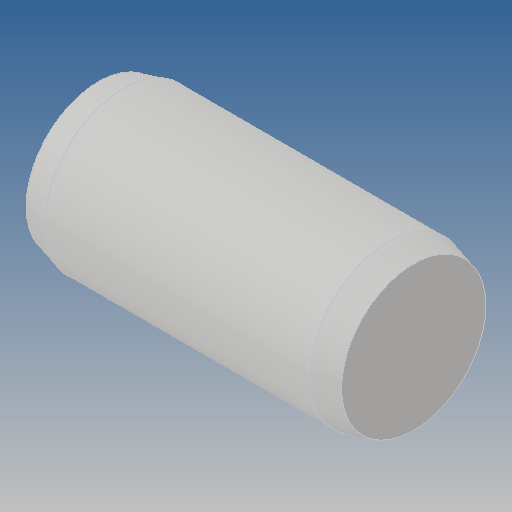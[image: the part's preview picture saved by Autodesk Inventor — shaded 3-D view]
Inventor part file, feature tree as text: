
AUTODESK INVENTOR PART (.ipt)
format: ipt  version: 2018 (Build 220112000, 112)  size: 109,056 bytes
history: native  units: mm
features: extrude x1
ambient origin geometry x8: Origin, YZ Plane, XZ Plane, XY Plane, X Axis, Y Axis, Z Axis, Center Point
bodies: Solid1 (feature_tree)
feature tree (1):
  extrude  "Extrude3"  [1 undecoded]
note: 1 required parameter value undecoded (feature->parameter linkage not recoverable at this tier; creation-order binding heuristic only, values carry confidence <= 0.55)
